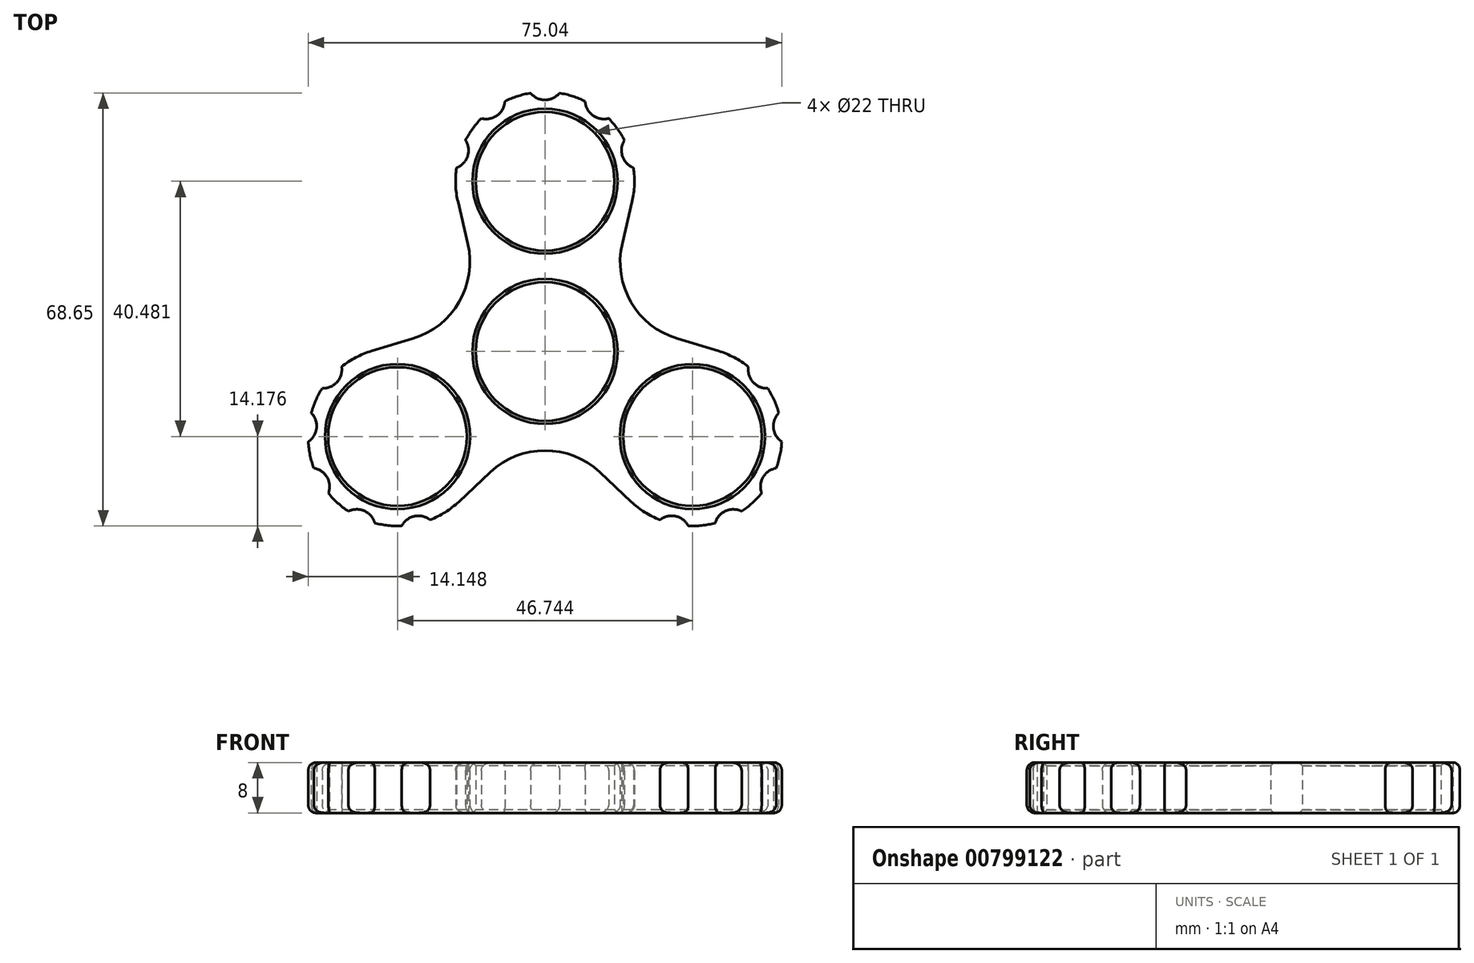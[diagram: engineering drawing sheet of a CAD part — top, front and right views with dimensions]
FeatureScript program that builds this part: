
annotation { "Feature Type Name" : "Feature", "Feature Type Description" : "" }
export const myFeature = defineFeature(function(context is Context, id is Id, definition is map)
    precondition{}
    {
        {
            var Q0;
            Q0=qCreatedBy(makeId("Top.planeOp"),FACE);
            var sketch = newSketch(context, id + "F0", { "sketchPlane" : qUnion([Q0])});
            skCircle(sketch, "E0", {"center": v(0, 0) * mm, "radius": 11 * mm});
            skCircle(sketch, "E1", {"center": v(0, 26.99) * mm, "radius": 11 * mm});
            skCircle(sketch, "E2.1.0", {"center": v(-23.37, -13.5) * mm, "radius": 11 * mm});
            skCircle(sketch, "E2.2.0", {"center": v(23.37, -13.5) * mm, "radius": 11 * mm});
            skCircle(sketch, "E3.0", {"center": v(0, 26.99) * mm, "radius": 14.18 * mm});
            skCircle(sketch, "E4.1.0", {"center": v(-23.37, -13.5) * mm, "radius": 14.18 * mm});
            skCircle(sketch, "E4.2.0", {"center": v(23.37, -13.5) * mm, "radius": 14.18 * mm});
            skLineSegment(sketch, "E5", {"start": v(0, 0) * mm, "end": v(0, 11) * mm, "construction": true});
            skLineSegment(sketch, "E6.1.0", {"start": v(0, 0) * mm, "end": v(-9.53, 5.5) * mm, "construction": true});
            skLineSegment(sketch, "E6.2.0", {"start": v(0, 0) * mm, "end": v(-9.53, -5.5) * mm, "construction": true});
            skLineSegment(sketch, "E6.3.0", {"start": v(0, 0) * mm, "end": v(0, -11) * mm, "construction": true});
            skLineSegment(sketch, "E6.4.0", {"start": v(0, 0) * mm, "end": v(9.53, -5.5) * mm, "construction": true});
            skLineSegment(sketch, "E6.5.0", {"start": v(0, 0) * mm, "end": v(9.53, 5.5) * mm, "construction": true});
            skLineSegment(sketch, "E7", {"start": v(-12.24, 17.1) * mm, "end": v(-13.8, 23.76) * mm});
            skLineSegment(sketch, "E8", {"start": v(12.24, 17.1) * mm, "end": v(13.8, 23.76) * mm});
            skLineSegment(sketch, "E9.1.0", {"start": v(-8.7, -19.16) * mm, "end": v(-13.67, -23.83) * mm});
            skLineSegment(sketch, "E9.1.1", {"start": v(-20.93, 2.05) * mm, "end": v(-27.47, 0.07) * mm});
            skLineSegment(sketch, "E9.2.0", {"start": v(20.93, 2.05) * mm, "end": v(27.47, 0.07) * mm});
            skLineSegment(sketch, "E9.2.1", {"start": v(8.7, -19.16) * mm, "end": v(13.67, -23.83) * mm});
            skPoint(sketch, "E10.visualSharp", {"position": v(-9.53, 5.5) * mm});
            skArc(sketch, "E10.filletArc", {"start": v(-20.93, 2.05) * mm, "mid": v(-13.61, 7.86) * mm, "end": v(-12.24, 17.1) * mm});
            skPoint(sketch, "E11.visualSharp", {"position": v(9.53, 5.5) * mm});
            skArc(sketch, "E11.filletArc", {"start": v(12.24, 17.1) * mm, "mid": v(13.61, 7.86) * mm, "end": v(20.93, 2.05) * mm});
            skPoint(sketch, "E12.visualSharp", {"position": v(0, -11) * mm});
            skArc(sketch, "E12.filletArc", {"start": v(8.7, -19.16) * mm, "mid": v(0, -15.72) * mm, "end": v(-8.7, -19.16) * mm});
            skSolve(sketch);
        }
        {
            var Q0;
            Q0 = qSketchRegion(id + "F0", true);
            extrude(context, id + "F1", {"entities" : qUnion([Q0]), "depth" : 8 * mm, "offsetDistance" : 25.4 * mm});
        }
        {
            var Q0;
            Q0=makeQuery(id+"F1.opExtrude","CAP_EDGE",EDGE,{"disambiguationData":[OSD([sQuery(id+"F0.wireOp",EDGE,"E1")])],"isStart":false});
            var Q1;
            Q1=makeQuery(id+"F1.opExtrude","CAP_EDGE",EDGE,{"disambiguationData":[OSD([sQuery(id+"F0.wireOp",EDGE,"E0")])],"isStart":false});
            var Q2;
            Q2=makeQuery(id+"F1.opExtrude","CAP_EDGE",EDGE,{"disambiguationData":[OSD([sQuery(id+"F0.wireOp",EDGE,"E2.2.0")])],"isStart":false});
            var Q3;
            Q3=makeQuery(id+"F1.opExtrude","CAP_EDGE",EDGE,{"disambiguationData":[OSD([sQuery(id+"F0.wireOp",EDGE,"E2.1.0")])],"isStart":false});
            var Q4;
            Q4=makeQuery(id+"F1.opExtrude","CAP_EDGE",EDGE,{"disambiguationData":[OSD([sQuery(id+"F0.wireOp",EDGE,"E0")])],"isStart":true});
            var Q5;
            Q5=makeQuery(id+"F1.opExtrude","CAP_EDGE",EDGE,{"disambiguationData":[OSD([sQuery(id+"F0.wireOp",EDGE,"E2.1.0")])],"isStart":true});
            var Q6;
            Q6=makeQuery(id+"F1.opExtrude","CAP_EDGE",EDGE,{"disambiguationData":[OSD([sQuery(id+"F0.wireOp",EDGE,"E1")])],"isStart":true});
            var Q7;
            Q7=makeQuery(id+"F1.opExtrude","CAP_EDGE",EDGE,{"disambiguationData":[OSD([sQuery(id+"F0.wireOp",EDGE,"E2.2.0")])],"isStart":true});
            chamfer(context, id + "F2", {"entities" : qUnion([Q0, Q1, Q2, Q3, Q4, Q5, Q6, Q7]), "width" : 0.5 * mm, "tangentPropagation" : true});
        }
        {
            var Q0;
            Q0=makeQuery(id+"F1.opExtrude","SWEPT_FACE",FACE,{"disambiguationData":[OSD([sQuery(id+"F0.wireOp",EDGE,"E3.0")])]});
            fillet(context, id + "F3", {"entities" : qUnion([Q0]), "radius" : 1.27 * mm, "tangentPropagation" : true, "allowEdgeOverflow" : false});
        }
        {
            var Q0;
            Q0=makeQuery(id+"F1.opExtrude","CAP_FACE",FACE,{"disambiguationData":[OSD([sQuery(id+"F0.wireOp",EDGE,"E0"),sQuery(id+"F0.wireOp",EDGE,"E1"),sQuery(id+"F0.wireOp",EDGE,"E2.1.0"),sQuery(id+"F0.wireOp",EDGE,"E2.2.0"),sQuery(id+"F0.wireOp",EDGE,"E3.0"),sQuery(id+"F0.wireOp",EDGE,"E4.1.0"),sQuery(id+"F0.wireOp",EDGE,"E4.2.0"),sQuery(id+"F0.wireOp",EDGE,"E7"),sQuery(id+"F0.wireOp",EDGE,"E8"),sQuery(id+"F0.wireOp",EDGE,"E9.1.0"),sQuery(id+"F0.wireOp",EDGE,"E9.1.1"),sQuery(id+"F0.wireOp",EDGE,"E9.2.0"),sQuery(id+"F0.wireOp",EDGE,"E9.2.1"),sQuery(id+"F0.wireOp",EDGE,"E10.filletArc"),sQuery(id+"F0.wireOp",EDGE,"E11.filletArc"),sQuery(id+"F0.wireOp",EDGE,"E12.filletArc")])],"isStart":true});
            var sketch = newSketch(context, id + "F4", { "sketchPlane" : qUnion([Q0])});
            skLineSegment(sketch, "E13", {"start": v(-23.37, 13.5) * mm, "end": v(-37.12, 21.43) * mm, "construction": true});
            skLineSegment(sketch, "E14", {"start": v(-23.37, 13.5) * mm, "end": v(-29.83, 28) * mm, "construction": true});
            skLineSegment(sketch, "E15", {"start": v(-23.37, 13.5) * mm, "end": v(-20.07, 29.02) * mm, "construction": true});
            skLineSegment(sketch, "E16", {"start": v(-23.37, 13.5) * mm, "end": v(-39.16, 11.83) * mm, "construction": true});
            skLineSegment(sketch, "E17", {"start": v(-23.37, 13.5) * mm, "end": v(-35.17, 2.87) * mm, "construction": true});
            skCircle(sketch, "E18", {"center": v(-20.07, 29.02) * mm, "radius": 2.97 * mm});
            skCircle(sketch, "E19", {"center": v(-29.83, 28) * mm, "radius": 2.97 * mm});
            skCircle(sketch, "E20", {"center": v(-37.12, 21.43) * mm, "radius": 2.97 * mm});
            skCircle(sketch, "E21", {"center": v(-39.16, 11.83) * mm, "radius": 2.97 * mm});
            skCircle(sketch, "E22", {"center": v(-35.17, 2.87) * mm, "radius": 2.97 * mm});
            skCircle(sketch, "E23.1.0", {"center": v(-15.1, -31.9) * mm, "radius": 2.97 * mm});
            skCircle(sketch, "E23.1.1", {"center": v(-9.33, -39.83) * mm, "radius": 2.97 * mm});
            skCircle(sketch, "E23.1.2", {"center": v(0, -42.86) * mm, "radius": 2.97 * mm});
            skCircle(sketch, "E23.1.3", {"center": v(9.33, -39.83) * mm, "radius": 2.97 * mm});
            skCircle(sketch, "E23.1.4", {"center": v(15.1, -31.9) * mm, "radius": 2.97 * mm});
            skCircle(sketch, "E23.2.0", {"center": v(35.17, 2.87) * mm, "radius": 2.97 * mm});
            skCircle(sketch, "E23.2.1", {"center": v(39.16, 11.83) * mm, "radius": 2.97 * mm});
            skCircle(sketch, "E23.2.2", {"center": v(37.12, 21.43) * mm, "radius": 2.97 * mm});
            skCircle(sketch, "E23.2.3", {"center": v(29.83, 28) * mm, "radius": 2.97 * mm});
            skCircle(sketch, "E23.2.4", {"center": v(20.07, 29.02) * mm, "radius": 2.97 * mm});
            skPoint(sketch, "E23.center", {"position": v(0, 0) * mm});
            skSolve(sketch);
        }
        {
            var Q0;
            Q0 = qSketchRegion(id + "F4", true);
            extrude(context, id + "F5", {"entities" : qUnion([Q0]), "operationType" : NewBodyOperationType.REMOVE, "oppositeDirection" : true, "depth" : 25.4 * mm, "offsetDistance" : 25.4 * mm});
        }
    });
